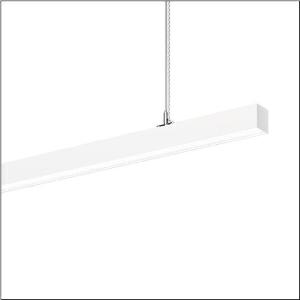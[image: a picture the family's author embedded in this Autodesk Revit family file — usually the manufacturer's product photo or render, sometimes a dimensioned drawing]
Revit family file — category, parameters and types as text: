
# Revit family: silica_r__21_51mx33dc4dwb_294c
name_source: partatom
category: Lighting Fixtures
units: mm (PartAtom-declared; Revit-internal decimal feet)

## family parameters
Cut with Voids When Loaded = No
Host = Face
Light Source = No
Part Type = Normal
Room Calculation Point = No
Round Connector Dimension = Use Diameter
Shared = No

## types (1)
- --- (1 x LED, 14790 lm, 93.9 W, 4000K)
    Apparent Load = 94 VA
    CIE Flux Codes = 78 96 99 55 100
    Color Rendering = 80
    Color Temperature = 4000K
    Default Elevation = 1800 mm
    Description = Silica® 21, office luminaire, primary optical cover: prismatic diffuser, of PMMA, CAT 2 (L<= 3000cd/m²), light emission: direct/indirect distribution, primary light characteristic: symmetric, installation type: suspended mounting, LED, rated luminous flux: 14.790lm, luminous efficacy: 158lm/W, light colour: 840, colour temperature: 4000K, with terminal, 3+2-pole, max. 2.5mm², mains connection: 220..240V, AC, 50/60Hz, rated input power: 93.9W, luminaire housing, of aluminium, traffic white (RAL 9016), length: 3.004mm, width: 53mm, height: 53mm, protection rating (complete): IP20, insulation class (complete): insulation class I (protective earthing), certification: CE, permissible operating ambient temperature: 0..+35°C, standard: EN 50419, packaging unit: 1 piece
    Height = 53 mm
    Lamp = 1 x LED
    Lamp Light Flux = 14790 lm
    Lamp Power = 93.9 W
    Lamp count = 1
    Length = 3004 mm
    Luminous efficacy = 158 lm/W
    Manufacturer = Siteco
    ModVariant = No
    Model = 51MX33DC4DWB
    Mounting Place = Ceiling
    Mounting Type = Pendant
    Number of Poles = 1
    OnlyDefault = Yes
    Power Factor = 1
    Product Name = Silica® 21
    Product group = office luminaire | ceiling pendant
    ProductGroupID = 902
    Protection Class = Protection class I
    Protection Degree = IP 20
    RLX_Detail_Level = 1
    RLX_Emergency_Light_Flux = 0 lm
    RLX_Emergency_Type = 0
    RLX_Emergency_Type_DB = No
    RlxData = <blob elided: 21405 chars, md5=36e3ed68>
    Socket = socket
    Standby Power = 0 W
    System Light Flux = 14790 lm
    System Power = 94 W
    Type Comments = factory setting: luminous flux: 100 % | dim-lin: 254 | 323 mA
    Type Image = l_1313629.jpg
    URL = http://relux.com
    VarID = @adj_067353
    Voltage = 0 V
    Weight = 0.00 kg
    Width = 53 mm

## geometry (parser evidence)
native form markers: Blend x4, Sweep x12
no freeform markers — native parametric forms only
